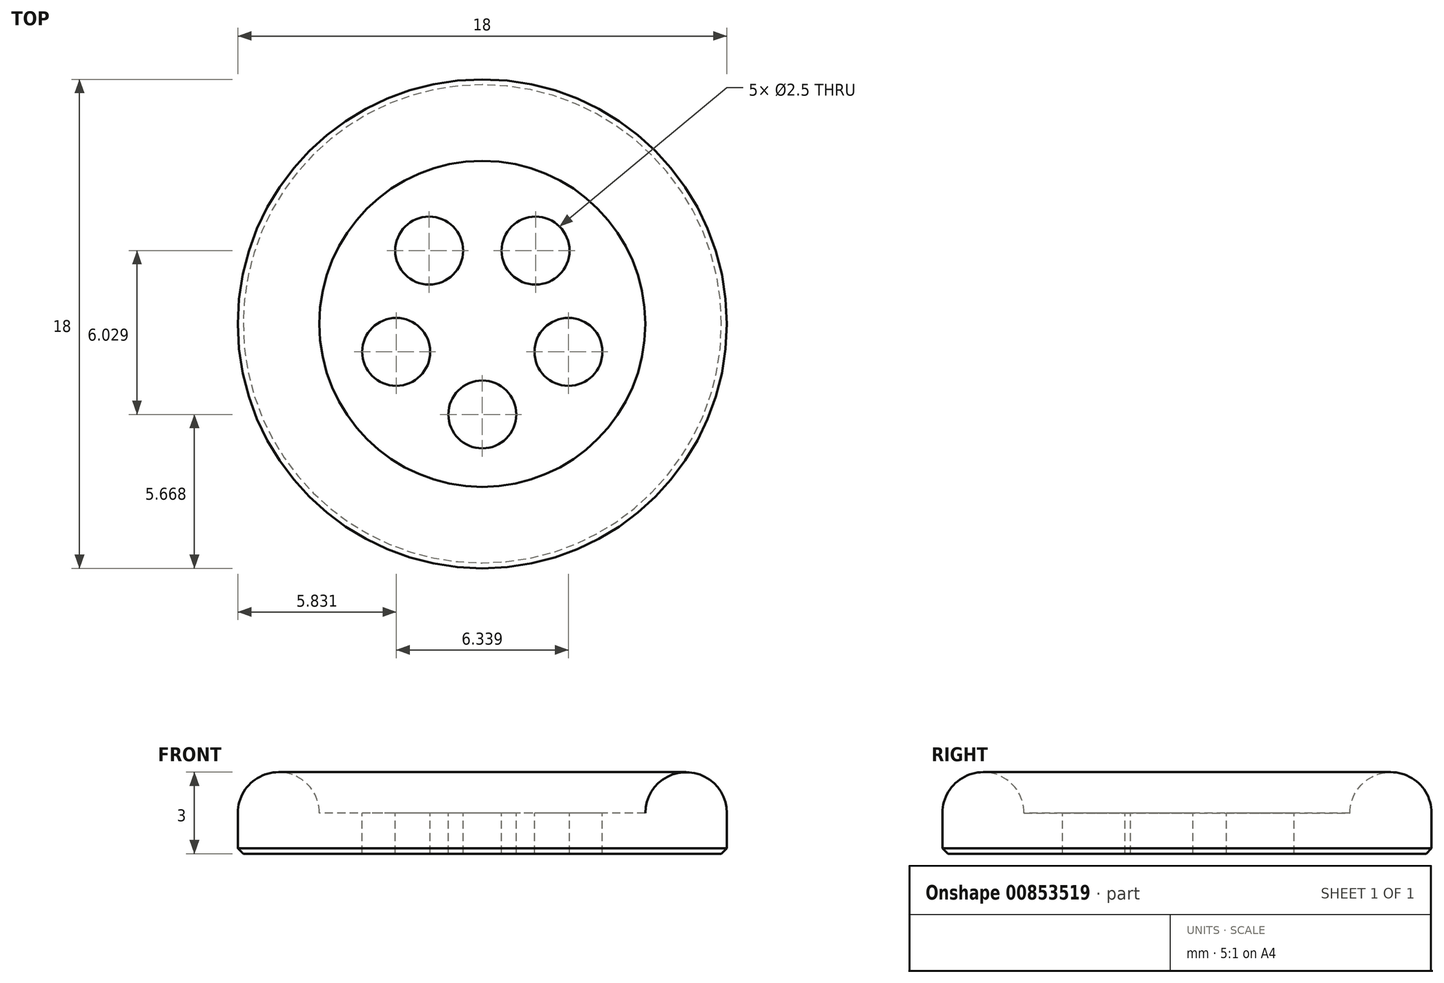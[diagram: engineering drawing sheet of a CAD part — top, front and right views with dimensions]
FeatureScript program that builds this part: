
annotation { "Feature Type Name" : "Feature", "Feature Type Description" : "" }
export const myFeature = defineFeature(function(context is Context, id is Id, definition is map)
    precondition{}
    {
        {
            var Q0;
            Q0=qCreatedBy(makeId("Front.planeOp"),FACE);
            var sketch = newSketch(context, id + "F0", { "sketchPlane" : qUnion([Q0])});
            skLineSegment(sketch, "E0.bottom", {"start": v(9, 1.5) * mm, "end": v(-9, 1.5) * mm, "construction": true});
            skLineSegment(sketch, "E0.top", {"start": v(9, -1.5) * mm, "end": v(-9, -1.5) * mm});
            skLineSegment(sketch, "E0.left", {"start": v(9, 1.5) * mm, "end": v(9, -1.5) * mm});
            skLineSegment(sketch, "E0.right", {"start": v(-9, 1.5) * mm, "end": v(-9, -1.5) * mm, "construction": true});
            skPoint(sketch, "E0.middle", {"position": v(0, 0) * mm});
            skLineSegment(sketch, "E1", {"start": v(0, 1.5) * mm, "end": v(0, -1.5) * mm});
            skCircle(sketch, "E2", {"center": v(7.5, 0) * mm, "radius": 1.5 * mm});
            skLineSegment(sketch, "E3", {"start": v(0, 0) * mm, "end": v(7.5, 0) * mm});
            skSolve(sketch);
        }
        {
            var Q0;
            Q0 = qSketchRegion(id + "F0", true);
            var Q1;
            Q1=sQuery(id+"F0.wireOp",EDGE,"E1");
            revolve(context, id + "F1", {"surfaceOperationType" : NewSurfaceOperationType.NEW, "entities" : qUnion([Q0]), "axis" : qUnion([Q1]), "revolveType" : RevolveType.FULL});
        }
        {
            var Q0;
            Q0=makeQuery(id+"F1.opRevolve","SWEPT_EDGE",EDGE,{"disambiguationData":[OSD([sQuery(id+"F0.wireOp",EDGE,"E0.top"),sQuery(id+"F0.wireOp",EDGE,"E0.left")])]});
            chamfer(context, id + "F2", {"entities" : qUnion([Q0]), "width" : 0.2 * mm, "tangentPropagation" : true});
        }
        {
            var Q0;
            Q0=makeQuery(id+"F1.opRevolve","SWEPT_FACE",FACE,{"disambiguationData":[OSD([sQuery(id+"F0.wireOp",EDGE,"E3")])]});
            var sketch = newSketch(context, id + "F3", { "sketchPlane" : qUnion([Q0])});
            skCircle(sketch, "E4.cCircle", {"center": v(0, 0) * mm, "radius": 2.7 * mm, "construction": true});
            skLineSegment(sketch, "E4.0", {"start": v(-1.96, 2.7) * mm, "end": v(1.96, 2.7) * mm, "construction": true});
            skLineSegment(sketch, "E4.1", {"start": v(1.96, 2.7) * mm, "end": v(3.17, -1.03) * mm, "construction": true});
            skLineSegment(sketch, "E4.2", {"start": v(3.17, -1.03) * mm, "end": v(0, -3.33) * mm, "construction": true});
            skLineSegment(sketch, "E4.3", {"start": v(0, -3.33) * mm, "end": v(-3.17, -1.03) * mm, "construction": true});
            skLineSegment(sketch, "E4.4", {"start": v(-3.17, -1.03) * mm, "end": v(-1.96, 2.7) * mm, "construction": true});
            skPoint(sketch, "E4.0.midPoint", {"position": v(0, 2.7) * mm});
            skCircle(sketch, "E5", {"center": v(-1.96, 2.7) * mm, "radius": 1.25 * mm});
            skCircle(sketch, "E6", {"center": v(1.96, 2.7) * mm, "radius": 1.25 * mm});
            skCircle(sketch, "E7", {"center": v(3.17, -1.03) * mm, "radius": 1.25 * mm});
            skCircle(sketch, "E8", {"center": v(0, -3.33) * mm, "radius": 1.25 * mm});
            skCircle(sketch, "E9", {"center": v(-3.17, -1.03) * mm, "radius": 1.25 * mm});
            skLineSegment(sketch, "E10", {"start": v(0, -4.58) * mm, "end": v(0, -6) * mm, "construction": true});
            skLineSegment(sketch, "E11", {"start": v(1.01, -2.6) * mm, "end": v(2.16, -1.76) * mm, "construction": true});
            skSolve(sketch);
        }
        {
            var Q0;
            Q0 = qSketchRegion(id + "F3", true);
            extrude(context, id + "F4", {"entities" : qUnion([Q0]), "operationType" : NewBodyOperationType.REMOVE, "endBound" : BoundingType.THROUGH_ALL, "oppositeDirection" : true, "depth" : 25 * mm, "offsetDistance" : 25 * mm});
        }
    });
